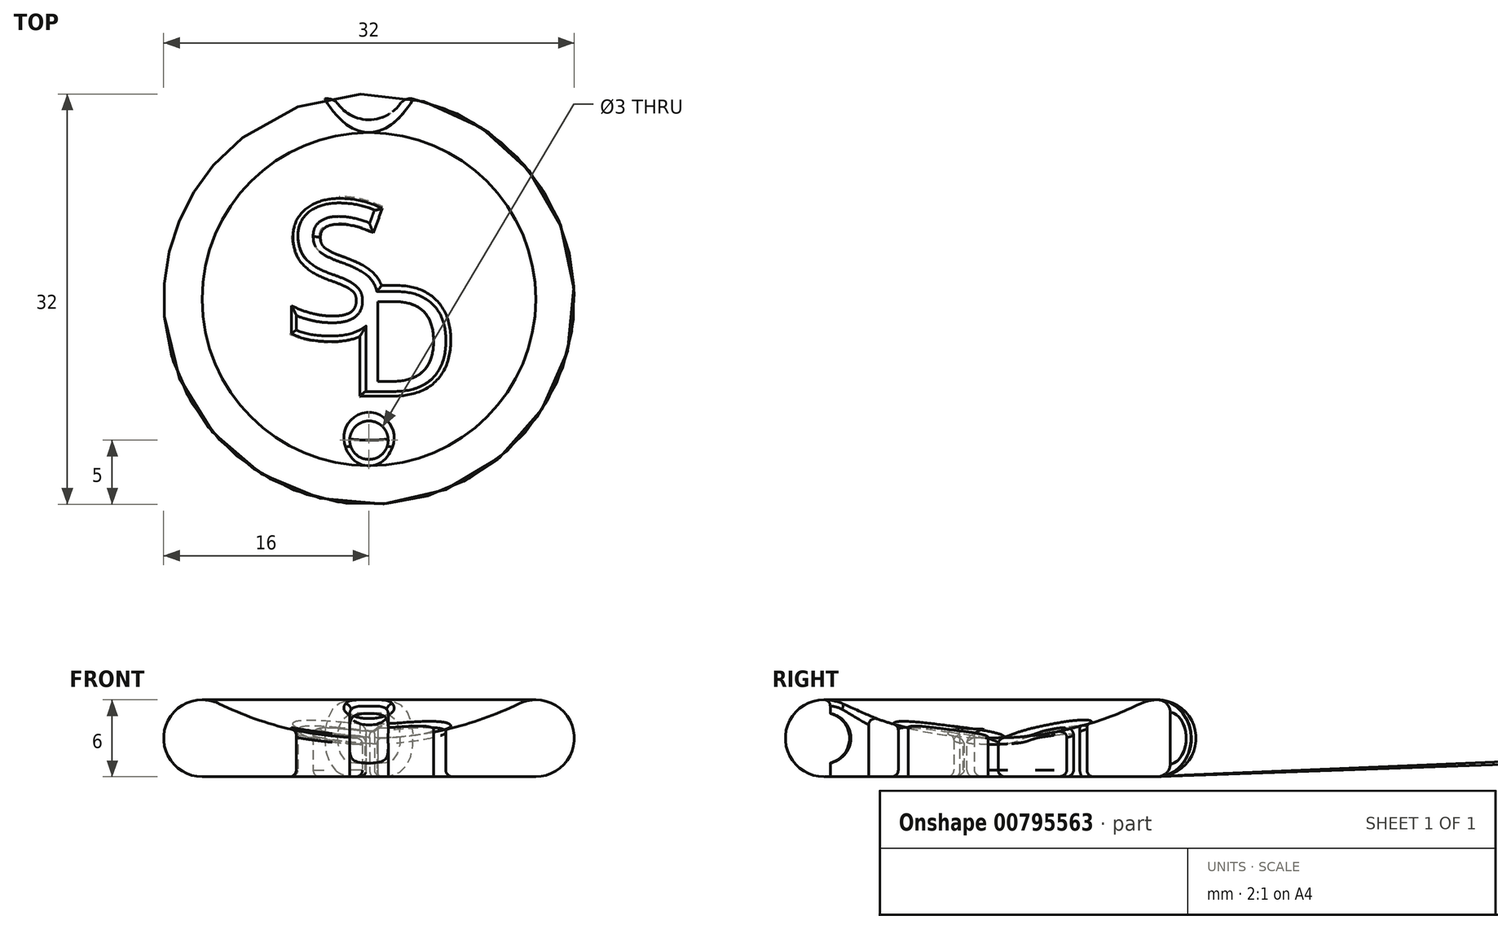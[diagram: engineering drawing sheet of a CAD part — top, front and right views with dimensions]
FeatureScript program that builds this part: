
annotation { "Feature Type Name" : "Feature", "Feature Type Description" : "" }
export const myFeature = defineFeature(function(context is Context, id is Id, definition is map)
    precondition{}
    {
        {
            var Q0;
            Q0=qCreatedBy(makeId("Front.planeOp"),FACE);
            var sketch = newSketch(context, id + "F0", { "sketchPlane" : qUnion([Q0])});
            skArc(sketch, "E0", {"start": v(-11.69, 5.7) * mm, "mid": v(-15.92, 3.67) * mm, "end": v(-13, 0) * mm});
            skArc(sketch, "E1", {"start": v(-11.69, 5.7) * mm, "mid": v(-6, 3.68) * mm, "end": v(0, 3) * mm});
            skLineSegment(sketch, "E2", {"start": v(-13, 0) * mm, "end": v(0, 0) * mm});
            skLineSegment(sketch, "E3", {"start": v(0, 0) * mm, "end": v(0, 3) * mm});
            skSolve(sketch);
        }
        {
            var Q0;
            Q0=makeQuery(id+"F0.imprint","IMPRINT",FACE,{"disambiguationData":[TD([[makeQuery(id+"F0.imprint","IMPRINT",EDGE,{"derivedFrom":sQuery(id+"F0.wireOp",EDGE,"E0")}),1.0]])]});
            var Q1;
            Q1=sQuery(id+"F0.wireOp",EDGE,"E3");
            revolve(context, id + "F1", {"surfaceOperationType" : NewSurfaceOperationType.NEW, "entities" : qUnion([Q0]), "axis" : qUnion([Q1]), "revolveType" : RevolveType.FULL});
        }
        {
            var Q0;
            Q0=qCreatedBy(makeId("Top.planeOp"),FACE);
            var sketch = newSketch(context, id + "F2", { "sketchPlane" : qUnion([Q0])});
            skCircle(sketch, "E4", {"center": v(0, 17) * mm, "radius": 3 * mm});
            skSolve(sketch);
        }
        {
            var Q0;
            Q0=qCreatedBy(makeId("Front.planeOp"),FACE);
            var sketch = newSketch(context, id + "F3", { "sketchPlane" : qUnion([Q0])});
            skCircle(sketch, "E5", {"center": v(-13, 3) * mm, "radius": 2 * mm});
            skSolve(sketch);
        }
        {
            var Q0;
            Q0=qCreatedBy(makeId("Top.planeOp"),FACE);
            var sketch = newSketch(context, id + "F4", { "sketchPlane" : qUnion([Q0])});
            skCircle(sketch, "E6", {"center": v(0, -11) * mm, "radius": 1.5 * mm});
            skSolve(sketch);
        }
        {
            var Q0;
            Q0 = qSketchRegion(id + "F4", true);
            extrude(context, id + "F5", {"entities" : qUnion([Q0]), "operationType" : NewBodyOperationType.REMOVE, "depth" : 6 * mm, "offsetDistance" : 25 * mm});
        }
        {
            var Q0;
            Q0=makeQuery(id+"F5.boolean.opBoolean","INTERSECT",EDGE,{"derivedFrom":[makeQuery(id+"F1.opRevolve","SWEPT_FACE",FACE,{"disambiguationData":[OSD([sQuery(id+"F0.wireOp",EDGE,"E1")])]}),makeQuery(id+"F5.opExtrude","SWEPT_FACE",FACE,{"disambiguationData":[OSD([sQuery(id+"F4.wireOp",EDGE,"E6")])]})]});
            var Q1;
            Q1=makeQuery(id+"F5.boolean.opBoolean","INTERSECT",EDGE,{"derivedFrom":[makeQuery(id+"F1.opRevolve","SWEPT_FACE",FACE,{"disambiguationData":[OSD([sQuery(id+"F0.wireOp",EDGE,"E0")])]}),makeQuery(id+"F5.opExtrude","SWEPT_FACE",FACE,{"disambiguationData":[OSD([sQuery(id+"F4.wireOp",EDGE,"E6")])]})]});
            var Q2;
            Q2=makeQuery(id+"F5.boolean.opBoolean","COPY",EDGE,{"derivedFrom":makeQuery(id+"F5.opExtrude","CAP_EDGE",EDGE,{"disambiguationData":[OSD([sQuery(id+"F4.wireOp",EDGE,"E6")])],"isStart":true})});
            fillet(context, id + "F6", {"entities" : qUnion([Q0, Q1, Q2]), "radius" : 0.5 * mm, "tangentPropagation" : true, "allowEdgeOverflow" : false});
        }
        {
            var Q0;
            Q0 = qSketchRegion(id + "F3", true);
            var Q1;
            Q1=sQuery(id+"F0.wireOp",EDGE,"E3");
            revolve(context, id + "F7", {"operationType" : NewBodyOperationType.ADD, "surfaceOperationType" : NewSurfaceOperationType.NEW, "entities" : qUnion([Q0]), "axis" : qUnion([Q1]), "revolveType" : RevolveType.FULL});
        }
        {
            var Q0;
            Q0 = qSketchRegion(id + "F2", true);
            extrude(context, id + "F8", {"entities" : qUnion([Q0]), "operationType" : NewBodyOperationType.REMOVE, "depth" : 6 * mm, "offsetDistance" : 25 * mm});
        }
        {
            var Q0;
            Q0=makeQuery(id+"F8.boolean.opBoolean","INTERSECT",EDGE,{"derivedFrom":[makeQuery(id+"F1.opRevolve","SWEPT_FACE",FACE,{"disambiguationData":[OSD([sQuery(id+"F0.wireOp",EDGE,"E0")])]}),makeQuery(id+"F8.opExtrude","SWEPT_FACE",FACE,{"disambiguationData":[OSD([sQuery(id+"F2.wireOp",EDGE,"E4")])]})]});
            fillet(context, id + "F9", {"entities" : qUnion([Q0]), "radius" : 1 * mm, "tangentPropagation" : true, "allowEdgeOverflow" : false});
        }
        {
            var Q0;
            Q0=qCreatedBy(makeId("Top.planeOp"),FACE);
            var sketch = newSketch(context, id + "F10", { "sketchPlane" : qUnion([Q0])});
            skText(sketch, "E7", { "text": "S", "fontName": "OpenSans-Regular.ttf"});
            skText(sketch, "E8", { "text": "D", "fontName": "OpenSans-Regular.ttf"});
            const initialGuessF10  = {"E7": [-0.0064, -0.00273, 1, 0, 0.01018], "E8": [-0.0013, -0.0072, 1, 0, 0.00786]};
            skSetInitialGuess(sketch, initialGuessF10);
            skSolve(sketch);
        }
        {
            var Q0;
            Q0 = qSketchRegion(id + "F10", true);
            extrude(context, id + "F11", {"entities" : qUnion([Q0]), "operationType" : NewBodyOperationType.REMOVE, "depth" : 6 * mm, "offsetDistance" : 25 * mm});
        }
        {
            var Q0;
            Q0=makeQuery(id+"F11.boolean.opBoolean","INTERSECT",EDGE,{"derivedFrom":[makeQuery(id+"F1.opRevolve","SWEPT_FACE",FACE,{"disambiguationData":[OSD([sQuery(id+"F0.wireOp",EDGE,"E1")])]}),makeQuery(id+"F11.opExtrude","SWEPT_FACE",FACE,{"disambiguationData":[OSD([sQuery(id+"F10.wireOp",EDGE,"E7.sketch_text.stroke-7")])]})]});
            var Q1;
            Q1=makeQuery(id+"F11.boolean.opBoolean","INTERSECT",EDGE,{"derivedFrom":[makeQuery(id+"F1.opRevolve","SWEPT_FACE",FACE,{"disambiguationData":[OSD([sQuery(id+"F0.wireOp",EDGE,"E1")])]}),makeQuery(id+"F11.opExtrude","SWEPT_FACE",FACE,{"disambiguationData":[OSD([sQuery(id+"F10.wireOp",EDGE,"E7.sketch_text.stroke-6")])]})]});
            var Q2;
            Q2=makeQuery(id+"F11.boolean.opBoolean","INTERSECT",EDGE,{"derivedFrom":[makeQuery(id+"F1.opRevolve","SWEPT_FACE",FACE,{"disambiguationData":[OSD([sQuery(id+"F0.wireOp",EDGE,"E1")])]}),makeQuery(id+"F11.opExtrude","SWEPT_FACE",FACE,{"disambiguationData":[OSD([sQuery(id+"F10.wireOp",EDGE,"E7.sketch_text.stroke-4")])]})]});
            var Q3;
            Q3=makeQuery(id+"F11.boolean.opBoolean","INTERSECT",EDGE,{"derivedFrom":[makeQuery(id+"F1.opRevolve","SWEPT_FACE",FACE,{"disambiguationData":[OSD([sQuery(id+"F0.wireOp",EDGE,"E1")])]}),makeQuery(id+"F11.opExtrude","SWEPT_FACE",FACE,{"disambiguationData":[OSD([sQuery(id+"F10.wireOp",EDGE,"E7.sketch_text.stroke-5")])]})]});
            var Q4;
            Q4=makeQuery(id+"F11.boolean.opBoolean","INTERSECT",EDGE,{"derivedFrom":[makeQuery(id+"F1.opRevolve","SWEPT_FACE",FACE,{"disambiguationData":[OSD([sQuery(id+"F0.wireOp",EDGE,"E1")])]}),makeQuery(id+"F11.opExtrude","SWEPT_FACE",FACE,{"disambiguationData":[OSD([sQuery(id+"F10.wireOp",EDGE,"E7.sketch_text.stroke-3")])]})]});
            var Q5;
            Q5=makeQuery(id+"F11.boolean.opBoolean","INTERSECT",EDGE,{"derivedFrom":[makeQuery(id+"F1.opRevolve","SWEPT_FACE",FACE,{"disambiguationData":[OSD([sQuery(id+"F0.wireOp",EDGE,"E1")])]}),makeQuery(id+"F11.opExtrude","SWEPT_FACE",FACE,{"disambiguationData":[OSD([sQuery(id+"F10.wireOp",EDGE,"E7.sketch_text.stroke-2")])]})]});
            var Q6;
            Q6=makeQuery(id+"F11.boolean.opBoolean","INTERSECT",EDGE,{"derivedFrom":[makeQuery(id+"F1.opRevolve","SWEPT_FACE",FACE,{"disambiguationData":[OSD([sQuery(id+"F0.wireOp",EDGE,"E1")])]}),makeQuery(id+"F11.opExtrude","SWEPT_FACE",FACE,{"disambiguationData":[OSD([sQuery(id+"F10.wireOp",EDGE,"E7.sketch_text.stroke-1")])]})]});
            var Q7;
            Q7=makeQuery(id+"F11.boolean.opBoolean","INTERSECT",EDGE,{"derivedFrom":[makeQuery(id+"F1.opRevolve","SWEPT_FACE",FACE,{"disambiguationData":[OSD([sQuery(id+"F0.wireOp",EDGE,"E1")])]}),makeQuery(id+"F11.opExtrude","SWEPT_FACE",FACE,{"disambiguationData":[OSD([sQuery(id+"F10.wireOp",EDGE,"E8.sketch_text.stroke-3")])]})]});
            var Q8;
            Q8=makeQuery(id+"F11.boolean.opBoolean","INTERSECT",EDGE,{"derivedFrom":[makeQuery(id+"F1.opRevolve","SWEPT_FACE",FACE,{"disambiguationData":[OSD([sQuery(id+"F0.wireOp",EDGE,"E1")])]}),makeQuery(id+"F11.opExtrude","SWEPT_FACE",FACE,{"disambiguationData":[OSD([sQuery(id+"F10.wireOp",EDGE,"E8.sketch_text.stroke-2")])]})]});
            var Q9;
            Q9=makeQuery(id+"F11.boolean.opBoolean","INTERSECT",EDGE,{"derivedFrom":[makeQuery(id+"F1.opRevolve","SWEPT_FACE",FACE,{"disambiguationData":[OSD([sQuery(id+"F0.wireOp",EDGE,"E1")])]}),makeQuery(id+"F11.opExtrude","SWEPT_FACE",FACE,{"disambiguationData":[OSD([sQuery(id+"F10.wireOp",EDGE,"E8.sketch_text.stroke-1")])]})]});
            var Q10;
            Q10=makeQuery(id+"F11.boolean.opBoolean","INTERSECT",EDGE,{"derivedFrom":[makeQuery(id+"F1.opRevolve","SWEPT_FACE",FACE,{"disambiguationData":[OSD([sQuery(id+"F0.wireOp",EDGE,"E1")])]}),makeQuery(id+"F11.opExtrude","SWEPT_FACE",FACE,{"disambiguationData":[OSD([sQuery(id+"F10.wireOp",EDGE,"E8.sketch_text.stroke-0")])]})]});
            var Q11;
            Q11=makeQuery(id+"F11.boolean.opBoolean","INTERSECT",EDGE,{"derivedFrom":[makeQuery(id+"F1.opRevolve","SWEPT_FACE",FACE,{"disambiguationData":[OSD([sQuery(id+"F0.wireOp",EDGE,"E1")])]}),makeQuery(id+"F11.opExtrude","SWEPT_FACE",FACE,{"disambiguationData":[OSD([sQuery(id+"F10.wireOp",EDGE,"E8.sketch_text.stroke-6")])]})]});
            var Q12;
            Q12=makeQuery(id+"F11.boolean.opBoolean","INTERSECT",EDGE,{"derivedFrom":[makeQuery(id+"F1.opRevolve","SWEPT_FACE",FACE,{"disambiguationData":[OSD([sQuery(id+"F0.wireOp",EDGE,"E1")])]}),makeQuery(id+"F11.opExtrude","SWEPT_FACE",FACE,{"disambiguationData":[OSD([sQuery(id+"F10.wireOp",EDGE,"E8.sketch_text.stroke-5")])]})]});
            var Q13;
            Q13=makeQuery(id+"F11.boolean.opBoolean","INTERSECT",EDGE,{"derivedFrom":[makeQuery(id+"F1.opRevolve","SWEPT_FACE",FACE,{"disambiguationData":[OSD([sQuery(id+"F0.wireOp",EDGE,"E1")])]}),makeQuery(id+"F11.opExtrude","SWEPT_FACE",FACE,{"disambiguationData":[OSD([sQuery(id+"F10.wireOp",EDGE,"E8.sketch_text.stroke-4")])]})]});
            var Q14;
            Q14=makeQuery(id+"F11.boolean.opBoolean","INTERSECT",EDGE,{"derivedFrom":[makeQuery(id+"F1.opRevolve","SWEPT_FACE",FACE,{"disambiguationData":[OSD([sQuery(id+"F0.wireOp",EDGE,"E1")])]}),makeQuery(id+"F11.opExtrude","SWEPT_FACE",FACE,{"disambiguationData":[OSD([sQuery(id+"F10.wireOp",EDGE,"E7.sketch_text.stroke-24")])]})]});
            var Q15;
            Q15=makeQuery(id+"F11.boolean.opBoolean","INTERSECT",EDGE,{"derivedFrom":[makeQuery(id+"F1.opRevolve","SWEPT_FACE",FACE,{"disambiguationData":[OSD([sQuery(id+"F0.wireOp",EDGE,"E1")])]}),makeQuery(id+"F11.opExtrude","SWEPT_FACE",FACE,{"disambiguationData":[OSD([sQuery(id+"F10.wireOp",EDGE,"E7.sketch_text.stroke-23")])]})]});
            var Q16;
            Q16=makeQuery(id+"F11.boolean.opBoolean","INTERSECT",EDGE,{"derivedFrom":[makeQuery(id+"F1.opRevolve","SWEPT_FACE",FACE,{"disambiguationData":[OSD([sQuery(id+"F0.wireOp",EDGE,"E1")])]}),makeQuery(id+"F11.opExtrude","SWEPT_FACE",FACE,{"disambiguationData":[OSD([sQuery(id+"F10.wireOp",EDGE,"E7.sketch_text.stroke-22")])]})]});
            var Q17;
            Q17=makeQuery(id+"F11.boolean.opBoolean","INTERSECT",EDGE,{"derivedFrom":[makeQuery(id+"F1.opRevolve","SWEPT_FACE",FACE,{"disambiguationData":[OSD([sQuery(id+"F0.wireOp",EDGE,"E1")])]}),makeQuery(id+"F11.opExtrude","SWEPT_FACE",FACE,{"disambiguationData":[OSD([sQuery(id+"F10.wireOp",EDGE,"E7.sketch_text.stroke-21")])]})]});
            var Q18;
            Q18=makeQuery(id+"F11.boolean.opBoolean","INTERSECT",EDGE,{"derivedFrom":[makeQuery(id+"F1.opRevolve","SWEPT_FACE",FACE,{"disambiguationData":[OSD([sQuery(id+"F0.wireOp",EDGE,"E1")])]}),makeQuery(id+"F11.opExtrude","SWEPT_FACE",FACE,{"disambiguationData":[OSD([sQuery(id+"F10.wireOp",EDGE,"E7.sketch_text.stroke-20")])]})]});
            var Q19;
            Q19=makeQuery(id+"F11.boolean.opBoolean","INTERSECT",EDGE,{"derivedFrom":[makeQuery(id+"F1.opRevolve","SWEPT_FACE",FACE,{"disambiguationData":[OSD([sQuery(id+"F0.wireOp",EDGE,"E1")])]}),makeQuery(id+"F11.opExtrude","SWEPT_FACE",FACE,{"disambiguationData":[OSD([sQuery(id+"F10.wireOp",EDGE,"E7.sketch_text.stroke-19")])]})]});
            var Q20;
            Q20=makeQuery(id+"F11.boolean.opBoolean","INTERSECT",EDGE,{"derivedFrom":[makeQuery(id+"F1.opRevolve","SWEPT_FACE",FACE,{"disambiguationData":[OSD([sQuery(id+"F0.wireOp",EDGE,"E1")])]}),makeQuery(id+"F11.opExtrude","SWEPT_FACE",FACE,{"disambiguationData":[OSD([sQuery(id+"F10.wireOp",EDGE,"E7.sketch_text.stroke-18")])]})]});
            var Q21;
            Q21=makeQuery(id+"F11.boolean.opBoolean","INTERSECT",EDGE,{"derivedFrom":[makeQuery(id+"F1.opRevolve","SWEPT_FACE",FACE,{"disambiguationData":[OSD([sQuery(id+"F0.wireOp",EDGE,"E1")])]}),makeQuery(id+"F11.opExtrude","SWEPT_FACE",FACE,{"disambiguationData":[OSD([sQuery(id+"F10.wireOp",EDGE,"E7.sketch_text.stroke-17")])]})]});
            var Q22;
            Q22=makeQuery(id+"F11.boolean.opBoolean","INTERSECT",EDGE,{"derivedFrom":[makeQuery(id+"F1.opRevolve","SWEPT_FACE",FACE,{"disambiguationData":[OSD([sQuery(id+"F0.wireOp",EDGE,"E1")])]}),makeQuery(id+"F11.opExtrude","SWEPT_FACE",FACE,{"disambiguationData":[OSD([sQuery(id+"F10.wireOp",EDGE,"E7.sketch_text.stroke-16")])]})]});
            var Q23;
            Q23=makeQuery(id+"F11.boolean.opBoolean","INTERSECT",EDGE,{"derivedFrom":[makeQuery(id+"F1.opRevolve","SWEPT_FACE",FACE,{"disambiguationData":[OSD([sQuery(id+"F0.wireOp",EDGE,"E1")])]}),makeQuery(id+"F11.opExtrude","SWEPT_FACE",FACE,{"disambiguationData":[OSD([sQuery(id+"F10.wireOp",EDGE,"E7.sketch_text.stroke-15")])]})]});
            var Q24;
            Q24=makeQuery(id+"F11.boolean.opBoolean","INTERSECT",EDGE,{"derivedFrom":[makeQuery(id+"F1.opRevolve","SWEPT_FACE",FACE,{"disambiguationData":[OSD([sQuery(id+"F0.wireOp",EDGE,"E1")])]}),makeQuery(id+"F11.opExtrude","SWEPT_FACE",FACE,{"disambiguationData":[OSD([sQuery(id+"F10.wireOp",EDGE,"E7.sketch_text.stroke-14")])]})]});
            var Q25;
            Q25=makeQuery(id+"F11.boolean.opBoolean","INTERSECT",EDGE,{"derivedFrom":[makeQuery(id+"F1.opRevolve","SWEPT_FACE",FACE,{"disambiguationData":[OSD([sQuery(id+"F0.wireOp",EDGE,"E1")])]}),makeQuery(id+"F11.opExtrude","SWEPT_FACE",FACE,{"disambiguationData":[OSD([sQuery(id+"F10.wireOp",EDGE,"E7.sketch_text.stroke-13")])]})]});
            var Q26;
            Q26=makeQuery(id+"F11.boolean.opBoolean","INTERSECT",EDGE,{"derivedFrom":[makeQuery(id+"F1.opRevolve","SWEPT_FACE",FACE,{"disambiguationData":[OSD([sQuery(id+"F0.wireOp",EDGE,"E1")])]}),makeQuery(id+"F11.opExtrude","SWEPT_FACE",FACE,{"disambiguationData":[OSD([sQuery(id+"F10.wireOp",EDGE,"E7.sketch_text.stroke-12")])]})]});
            var Q27;
            Q27=makeQuery(id+"F11.boolean.opBoolean","INTERSECT",EDGE,{"derivedFrom":[makeQuery(id+"F1.opRevolve","SWEPT_FACE",FACE,{"disambiguationData":[OSD([sQuery(id+"F0.wireOp",EDGE,"E1")])]}),makeQuery(id+"F11.opExtrude","SWEPT_FACE",FACE,{"disambiguationData":[OSD([sQuery(id+"F10.wireOp",EDGE,"E7.sketch_text.stroke-11")])]})]});
            var Q28;
            Q28=makeQuery(id+"F11.boolean.opBoolean","INTERSECT",EDGE,{"derivedFrom":[makeQuery(id+"F1.opRevolve","SWEPT_FACE",FACE,{"disambiguationData":[OSD([sQuery(id+"F0.wireOp",EDGE,"E1")])]}),makeQuery(id+"F11.opExtrude","SWEPT_FACE",FACE,{"disambiguationData":[OSD([sQuery(id+"F10.wireOp",EDGE,"E7.sketch_text.stroke-10")])]})]});
            var Q29;
            Q29=makeQuery(id+"F11.boolean.opBoolean","INTERSECT",EDGE,{"derivedFrom":[makeQuery(id+"F1.opRevolve","SWEPT_FACE",FACE,{"disambiguationData":[OSD([sQuery(id+"F0.wireOp",EDGE,"E1")])]}),makeQuery(id+"F11.opExtrude","SWEPT_FACE",FACE,{"disambiguationData":[OSD([sQuery(id+"F10.wireOp",EDGE,"E7.sketch_text.stroke-9")])]})]});
            var Q30;
            Q30=makeQuery(id+"F11.boolean.opBoolean","INTERSECT",EDGE,{"derivedFrom":[makeQuery(id+"F1.opRevolve","SWEPT_FACE",FACE,{"disambiguationData":[OSD([sQuery(id+"F0.wireOp",EDGE,"E1")])]}),makeQuery(id+"F11.opExtrude","SWEPT_FACE",FACE,{"disambiguationData":[OSD([sQuery(id+"F10.wireOp",EDGE,"E7.sketch_text.stroke-8")])]})]});
            var Q31;
            Q31=makeQuery(id+"F11.boolean.opBoolean","COPY",EDGE,{"derivedFrom":makeQuery(id+"F11.opExtrude","CAP_EDGE",EDGE,{"disambiguationData":[OSD([sQuery(id+"F10.wireOp",EDGE,"E8.sketch_text.stroke-3")])],"isStart":true})});
            var Q32;
            Q32=makeQuery(id+"F11.boolean.opBoolean","COPY",EDGE,{"derivedFrom":makeQuery(id+"F11.opExtrude","CAP_EDGE",EDGE,{"disambiguationData":[OSD([sQuery(id+"F10.wireOp",EDGE,"E8.sketch_text.stroke-2")])],"isStart":true})});
            var Q33;
            Q33=makeQuery(id+"F11.boolean.opBoolean","COPY",EDGE,{"derivedFrom":makeQuery(id+"F11.opExtrude","CAP_EDGE",EDGE,{"disambiguationData":[OSD([sQuery(id+"F10.wireOp",EDGE,"E8.sketch_text.stroke-0")])],"isStart":true})});
            var Q34;
            Q34=makeQuery(id+"F11.boolean.opBoolean","COPY",EDGE,{"derivedFrom":makeQuery(id+"F11.opExtrude","CAP_EDGE",EDGE,{"disambiguationData":[OSD([sQuery(id+"F10.wireOp",EDGE,"E8.sketch_text.stroke-1")])],"isStart":true})});
            var Q35;
            Q35=makeQuery(id+"F11.boolean.opBoolean","COPY",EDGE,{"derivedFrom":makeQuery(id+"F11.opExtrude","CAP_EDGE",EDGE,{"disambiguationData":[OSD([sQuery(id+"F10.wireOp",EDGE,"E8.sketch_text.stroke-6")])],"isStart":true})});
            var Q36;
            Q36=makeQuery(id+"F11.boolean.opBoolean","COPY",EDGE,{"derivedFrom":makeQuery(id+"F11.opExtrude","CAP_EDGE",EDGE,{"disambiguationData":[OSD([sQuery(id+"F10.wireOp",EDGE,"E8.sketch_text.stroke-5")])],"isStart":true})});
            var Q37;
            Q37=makeQuery(id+"F11.boolean.opBoolean","COPY",EDGE,{"derivedFrom":makeQuery(id+"F11.opExtrude","CAP_EDGE",EDGE,{"disambiguationData":[OSD([sQuery(id+"F10.wireOp",EDGE,"E8.sketch_text.stroke-4")])],"isStart":true})});
            var Q38;
            Q38=makeQuery(id+"F11.boolean.opBoolean","COPY",EDGE,{"derivedFrom":makeQuery(id+"F11.opExtrude","CAP_EDGE",EDGE,{"disambiguationData":[OSD([sQuery(id+"F10.wireOp",EDGE,"E7.sketch_text.stroke-24")])],"isStart":true})});
            var Q39;
            Q39=makeQuery(id+"F11.boolean.opBoolean","COPY",EDGE,{"derivedFrom":makeQuery(id+"F11.opExtrude","CAP_EDGE",EDGE,{"disambiguationData":[OSD([sQuery(id+"F10.wireOp",EDGE,"E7.sketch_text.stroke-23")])],"isStart":true})});
            var Q40;
            Q40=makeQuery(id+"F11.boolean.opBoolean","COPY",EDGE,{"derivedFrom":makeQuery(id+"F11.opExtrude","CAP_EDGE",EDGE,{"disambiguationData":[OSD([sQuery(id+"F10.wireOp",EDGE,"E7.sketch_text.stroke-22")])],"isStart":true})});
            var Q41;
            Q41=makeQuery(id+"F11.boolean.opBoolean","COPY",EDGE,{"derivedFrom":makeQuery(id+"F11.opExtrude","CAP_EDGE",EDGE,{"disambiguationData":[OSD([sQuery(id+"F10.wireOp",EDGE,"E7.sketch_text.stroke-20")])],"isStart":true})});
            var Q42;
            Q42=makeQuery(id+"F11.boolean.opBoolean","COPY",EDGE,{"derivedFrom":makeQuery(id+"F11.opExtrude","CAP_EDGE",EDGE,{"disambiguationData":[OSD([sQuery(id+"F10.wireOp",EDGE,"E7.sketch_text.stroke-19")])],"isStart":true})});
            var Q43;
            Q43=makeQuery(id+"F11.boolean.opBoolean","COPY",EDGE,{"derivedFrom":makeQuery(id+"F11.opExtrude","CAP_EDGE",EDGE,{"disambiguationData":[OSD([sQuery(id+"F10.wireOp",EDGE,"E7.sketch_text.stroke-18")])],"isStart":true})});
            var Q44;
            Q44=makeQuery(id+"F11.boolean.opBoolean","COPY",EDGE,{"derivedFrom":makeQuery(id+"F11.opExtrude","CAP_EDGE",EDGE,{"disambiguationData":[OSD([sQuery(id+"F10.wireOp",EDGE,"E7.sketch_text.stroke-17")])],"isStart":true})});
            var Q45;
            Q45=makeQuery(id+"F11.boolean.opBoolean","COPY",EDGE,{"derivedFrom":makeQuery(id+"F11.opExtrude","CAP_EDGE",EDGE,{"disambiguationData":[OSD([sQuery(id+"F10.wireOp",EDGE,"E7.sketch_text.stroke-16")])],"isStart":true})});
            var Q46;
            Q46=makeQuery(id+"F11.boolean.opBoolean","COPY",EDGE,{"derivedFrom":makeQuery(id+"F11.opExtrude","CAP_EDGE",EDGE,{"disambiguationData":[OSD([sQuery(id+"F10.wireOp",EDGE,"E7.sketch_text.stroke-15")])],"isStart":true})});
            var Q47;
            Q47=makeQuery(id+"F11.boolean.opBoolean","COPY",EDGE,{"derivedFrom":makeQuery(id+"F11.opExtrude","CAP_EDGE",EDGE,{"disambiguationData":[OSD([sQuery(id+"F10.wireOp",EDGE,"E7.sketch_text.stroke-14")])],"isStart":true})});
            var Q48;
            Q48=makeQuery(id+"F11.boolean.opBoolean","COPY",EDGE,{"derivedFrom":makeQuery(id+"F11.opExtrude","CAP_EDGE",EDGE,{"disambiguationData":[OSD([sQuery(id+"F10.wireOp",EDGE,"E7.sketch_text.stroke-13")])],"isStart":true})});
            var Q49;
            Q49=makeQuery(id+"F11.boolean.opBoolean","COPY",EDGE,{"derivedFrom":makeQuery(id+"F11.opExtrude","CAP_EDGE",EDGE,{"disambiguationData":[OSD([sQuery(id+"F10.wireOp",EDGE,"E7.sketch_text.stroke-12")])],"isStart":true})});
            var Q50;
            Q50=makeQuery(id+"F11.boolean.opBoolean","COPY",EDGE,{"derivedFrom":makeQuery(id+"F11.opExtrude","CAP_EDGE",EDGE,{"disambiguationData":[OSD([sQuery(id+"F10.wireOp",EDGE,"E7.sketch_text.stroke-11")])],"isStart":true})});
            var Q51;
            Q51=makeQuery(id+"F11.boolean.opBoolean","COPY",EDGE,{"derivedFrom":makeQuery(id+"F11.opExtrude","CAP_EDGE",EDGE,{"disambiguationData":[OSD([sQuery(id+"F10.wireOp",EDGE,"E7.sketch_text.stroke-10")])],"isStart":true})});
            var Q52;
            Q52=makeQuery(id+"F11.boolean.opBoolean","COPY",EDGE,{"derivedFrom":makeQuery(id+"F11.opExtrude","CAP_EDGE",EDGE,{"disambiguationData":[OSD([sQuery(id+"F10.wireOp",EDGE,"E7.sketch_text.stroke-9")])],"isStart":true})});
            var Q53;
            Q53=makeQuery(id+"F11.boolean.opBoolean","COPY",EDGE,{"derivedFrom":makeQuery(id+"F11.opExtrude","CAP_EDGE",EDGE,{"disambiguationData":[OSD([sQuery(id+"F10.wireOp",EDGE,"E7.sketch_text.stroke-8")])],"isStart":true})});
            var Q54;
            Q54=makeQuery(id+"F11.boolean.opBoolean","COPY",EDGE,{"derivedFrom":makeQuery(id+"F11.opExtrude","CAP_EDGE",EDGE,{"disambiguationData":[OSD([sQuery(id+"F10.wireOp",EDGE,"E7.sketch_text.stroke-7")])],"isStart":true})});
            var Q55;
            Q55=makeQuery(id+"F11.boolean.opBoolean","COPY",EDGE,{"derivedFrom":makeQuery(id+"F11.opExtrude","CAP_EDGE",EDGE,{"disambiguationData":[OSD([sQuery(id+"F10.wireOp",EDGE,"E7.sketch_text.stroke-6")])],"isStart":true})});
            var Q56;
            Q56=makeQuery(id+"F11.boolean.opBoolean","COPY",EDGE,{"derivedFrom":makeQuery(id+"F11.opExtrude","CAP_EDGE",EDGE,{"disambiguationData":[OSD([sQuery(id+"F10.wireOp",EDGE,"E7.sketch_text.stroke-5")])],"isStart":true})});
            var Q57;
            Q57=makeQuery(id+"F11.boolean.opBoolean","COPY",EDGE,{"derivedFrom":makeQuery(id+"F11.opExtrude","CAP_EDGE",EDGE,{"disambiguationData":[OSD([sQuery(id+"F10.wireOp",EDGE,"E7.sketch_text.stroke-4")])],"isStart":true})});
            var Q58;
            Q58=makeQuery(id+"F11.boolean.opBoolean","COPY",EDGE,{"derivedFrom":makeQuery(id+"F11.opExtrude","CAP_EDGE",EDGE,{"disambiguationData":[OSD([sQuery(id+"F10.wireOp",EDGE,"E7.sketch_text.stroke-3")])],"isStart":true})});
            var Q59;
            Q59=makeQuery(id+"F11.boolean.opBoolean","COPY",EDGE,{"derivedFrom":makeQuery(id+"F11.opExtrude","CAP_EDGE",EDGE,{"disambiguationData":[OSD([sQuery(id+"F10.wireOp",EDGE,"E7.sketch_text.stroke-2")])],"isStart":true})});
            var Q60;
            Q60=makeQuery(id+"F11.boolean.opBoolean","COPY",EDGE,{"derivedFrom":makeQuery(id+"F11.opExtrude","CAP_EDGE",EDGE,{"disambiguationData":[OSD([sQuery(id+"F10.wireOp",EDGE,"E7.sketch_text.stroke-1")])],"isStart":true})});
            fillet(context, id + "F12", {"entities" : qUnion([Q0, Q1, Q2, Q3, Q4, Q5, Q6, Q7, Q8, Q9, Q10, Q11, Q12, Q13, Q14, Q15, Q16, Q17, Q18, Q19, Q20, Q21, Q22, Q23, Q24, Q25, Q26, Q27, Q28, Q29, Q30, Q31, Q32, Q33, Q34, Q35, Q36, Q37, Q38, Q39, Q40, Q41, Q42, Q43, Q44, Q45, Q46, Q47, Q48, Q49, Q50, Q51, Q52, Q53, Q54, Q55, Q56, Q57, Q58, Q59, Q60]), "radius" : 0.5 * mm, "tangentPropagation" : true, "allowEdgeOverflow" : false});
        }
    });
